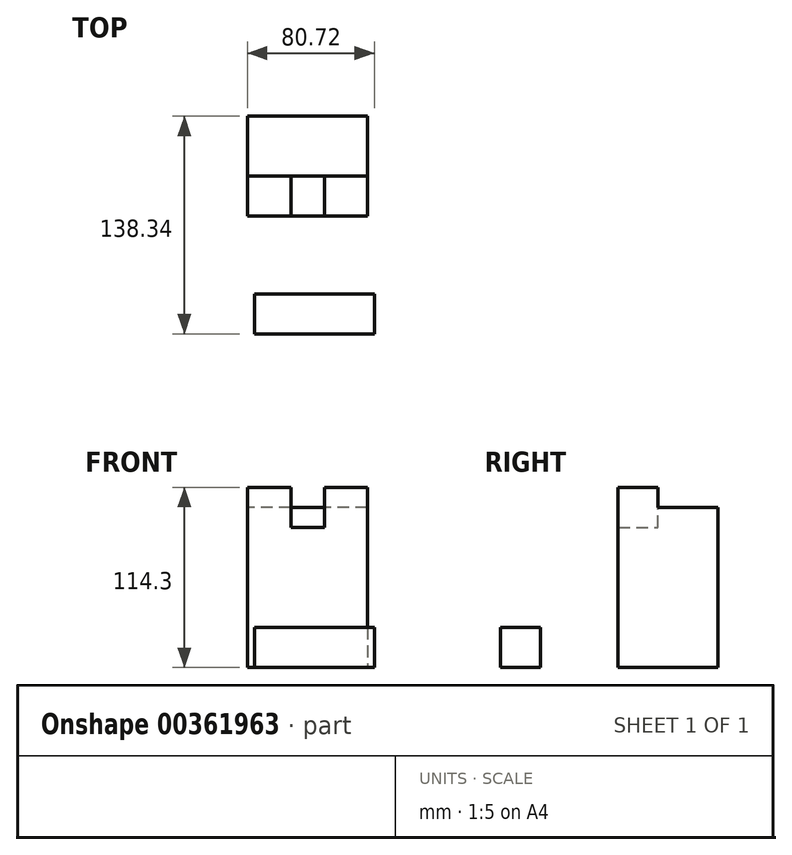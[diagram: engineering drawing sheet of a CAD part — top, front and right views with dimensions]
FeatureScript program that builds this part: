
annotation { "Feature Type Name" : "Feature", "Feature Type Description" : "" }
export const myFeature = defineFeature(function(context is Context, id is Id, definition is map)
    precondition{}
    {
        {
            var Q0;
            Q0=qCreatedBy(makeId("Top.planeOp"),FACE);
            var sketch = newSketch(context, id + "F0", { "sketchPlane" : qUnion([Q0])});
            skLineSegment(sketch, "E0", {"start": v(-38.85, 68.52) * mm, "end": v(37.35, 68.52) * mm});
            skLineSegment(sketch, "E1", {"start": v(-38.85, 68.52) * mm, "end": v(-38.85, 5.02) * mm});
            skLineSegment(sketch, "E2", {"start": v(-38.85, 5.02) * mm, "end": v(37.35, 5.02) * mm});
            skLineSegment(sketch, "E3", {"start": v(37.35, 68.52) * mm, "end": v(37.35, 5.02) * mm});
            skSolve(sketch);
        }
        {
            var Q0;
            Q0=qCreatedBy(makeId("Top.planeOp"),FACE);
            var sketch = newSketch(context, id + "F1", { "sketchPlane" : qUnion([Q0])});
            skLineSegment(sketch, "E4", {"start": v(-34.33, -44.42) * mm, "end": v(41.87, -44.42) * mm});
            skLineSegment(sketch, "E5", {"start": v(-34.33, -44.42) * mm, "end": v(-34.33, -69.82) * mm});
            skLineSegment(sketch, "E6", {"start": v(-34.33, -69.82) * mm, "end": v(41.87, -69.82) * mm});
            skLineSegment(sketch, "E7", {"start": v(41.87, -69.82) * mm, "end": v(41.87, -44.42) * mm});
            skSolve(sketch);
        }
        {
            var Q0;
            Q0=makeQuery(id+"F0.imprint","IMPRINT",FACE,{"disambiguationData":[TD([[makeQuery(id+"F0.imprint","IMPRINT",EDGE,{"derivedFrom":sQuery(id+"F0.wireOp",EDGE,"E0")}),-1.0]])]});
            extrude(context, id + "F2", {"entities" : qUnion([Q0]), "depth" : 114.3 * mm});
        }
        {
            var Q0;
            Q0=makeQuery(id+"F2.opExtrude","CAP_FACE",FACE,{"disambiguationData":[OSD([sQuery(id+"F0.wireOp",EDGE,"E0"),sQuery(id+"F0.wireOp",EDGE,"E1"),sQuery(id+"F0.wireOp",EDGE,"E2"),sQuery(id+"F0.wireOp",EDGE,"E3")])],"isStart":false});
            var sketch = newSketch(context, id + "F3", { "sketchPlane" : qUnion([Q0])});
            skLineSegment(sketch, "E8", {"start": v(-11.18, 5.02) * mm, "end": v(-11.18, 30.4) * mm});
            skLineSegment(sketch, "E9", {"start": v(-11.18, 30.4) * mm, "end": v(10.36, 30.4) * mm});
            skLineSegment(sketch, "E10", {"start": v(10.36, 30.4) * mm, "end": v(10.36, 5.02) * mm});
            skLineSegment(sketch, "E11", {"start": v(10.36, 5.02) * mm, "end": v(-11.18, 5.02) * mm});
            skSolve(sketch);
        }
        {
            var Q0;
            Q0=makeQuery(id+"F3.imprint","IMPRINT",FACE,{"disambiguationData":[TD([[makeQuery(id+"F3.imprint","IMPRINT",EDGE,{"derivedFrom":sQuery(id+"F3.wireOp",EDGE,"E8")}),-1.0]])]});
            extrude(context, id + "F4", {"entities" : qUnion([Q0]), "operationType" : NewBodyOperationType.REMOVE, "oppositeDirection" : true, "depth" : 25.4 * mm});
        }
        {
            var Q0;
            Q0=makeQuery(id+"F2.opExtrude","CAP_FACE",FACE,{"disambiguationData":[OSD([sQuery(id+"F0.wireOp",EDGE,"E0"),sQuery(id+"F0.wireOp",EDGE,"E1"),sQuery(id+"F0.wireOp",EDGE,"E2"),sQuery(id+"F0.wireOp",EDGE,"E3")])],"isStart":false});
            var sketch = newSketch(context, id + "F5", { "sketchPlane" : qUnion([Q0])});
            skLineSegment(sketch, "E12", {"start": v(-11.18, 30.4) * mm, "end": v(-38.85, 30.4) * mm});
            skLineSegment(sketch, "E13", {"start": v(-38.85, 30.4) * mm, "end": v(-38.85, 68.52) * mm});
            skLineSegment(sketch, "E14", {"start": v(-38.85, 68.52) * mm, "end": v(37.35, 68.52) * mm});
            skLineSegment(sketch, "E15", {"start": v(37.35, 68.52) * mm, "end": v(37.35, 30.4) * mm});
            skPoint(sketch, "E15.endSnap0", {"position": v(37.35, 36.77) * mm});
            skLineSegment(sketch, "E16", {"start": v(37.35, 30.4) * mm, "end": v(-11.18, 30.4) * mm});
            skSolve(sketch);
        }
        {
            var Q0;
            {var subQ1=sQuery(id+"F5.wireOp",EDGE,"E12");Q0=makeQuery(id+"F5.imprint","IMPRINT",FACE,{"disambiguationData":[TD([[makeQuery(id+"F5.imprint","IMPRINT",EDGE,{"derivedFrom":subQ1}),-1.0]])]});}
            extrude(context, id + "F6", {"entities" : qUnion([Q0]), "operationType" : NewBodyOperationType.REMOVE, "oppositeDirection" : true, "depth" : 12.7 * mm});
        }
        {
            var Q0;
            Q0=makeQuery(id+"F1.imprint","IMPRINT",FACE,{"disambiguationData":[TD([[makeQuery(id+"F1.imprint","IMPRINT",EDGE,{"derivedFrom":sQuery(id+"F1.wireOp",EDGE,"E4")}),-1.0]])]});
            extrude(context, id + "F7", {"entities" : qUnion([Q0]), "depth" : 25.4 * mm});
        }
    });
